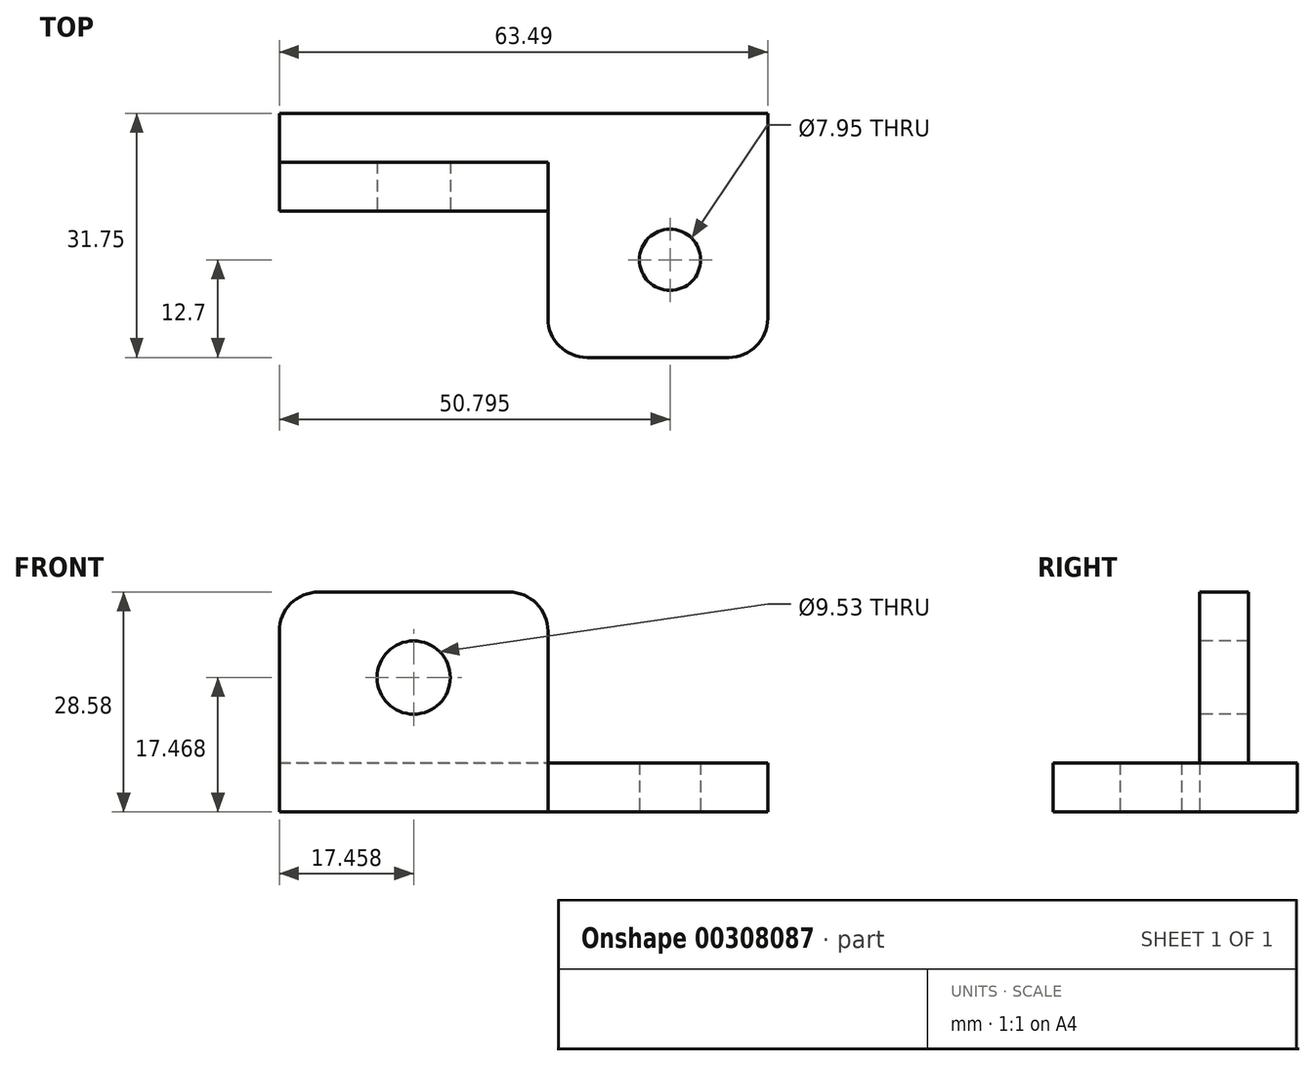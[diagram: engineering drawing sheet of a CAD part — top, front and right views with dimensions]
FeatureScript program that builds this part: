
annotation { "Feature Type Name" : "Feature", "Feature Type Description" : "" }
export const myFeature = defineFeature(function(context is Context, id is Id, definition is map)
    precondition{}
    {
        {
            var Q0;
            Q0=qCreatedBy(makeId("Top.planeOp"),FACE);
            var sketch = newSketch(context, id + "F0", { "sketchPlane" : qUnion([Q0])});
            skLineSegment(sketch, "E0", {"start": v(0, 0) * mm, "end": v(28.57, 0) * mm});
            skLineSegment(sketch, "E1", {"start": v(28.57, 0) * mm, "end": v(28.57, 31.75) * mm});
            skLineSegment(sketch, "E2", {"start": v(28.57, 31.75) * mm, "end": v(-34.92, 31.75) * mm});
            skLineSegment(sketch, "E3", {"start": v(-34.92, 31.75) * mm, "end": v(-34.92, 19.05) * mm});
            skLineSegment(sketch, "E4", {"start": v(-34.92, 19.05) * mm, "end": v(0, 19.05) * mm});
            skLineSegment(sketch, "E5", {"start": v(0, 19.05) * mm, "end": v(0, 0) * mm});
            skCircle(sketch, "E6", {"center": v(15.88, 12.7) * mm, "radius": 3.98 * mm});
            skSolve(sketch);
        }
        {
            var Q0;
            Q0=qSketchRegion(id+"F0",true);
            extrude(context, id + "F1", {"entities" : qUnion([Q0]), "endBound" : BoundingType.SYMMETRIC, "depth" : 6.35 * mm});
        }
        {
            var Q0;
            Q0=makeQuery(id+"F1.opExtrude","SWEPT_FACE",FACE,{"disambiguationData":[OSD([sQuery(id+"F0.wireOp",EDGE,"E4")])]});
            var sketch = newSketch(context, id + "F2", { "sketchPlane" : qUnion([Q0])});
            skLineSegment(sketch, "E7.bottom", {"start": v(-34.92, 3.18) * mm, "end": v(0, 3.18) * mm});
            skLineSegment(sketch, "E7.top", {"start": v(-34.92, 25.4) * mm, "end": v(0, 25.4) * mm});
            skLineSegment(sketch, "E7.left", {"start": v(-34.92, 3.18) * mm, "end": v(-34.92, 25.4) * mm});
            skLineSegment(sketch, "E7.right", {"start": v(0, 3.18) * mm, "end": v(0, 25.4) * mm});
            skCircle(sketch, "E8", {"center": v(-17.46, 14.29) * mm, "radius": 4.76 * mm});
            skSolve(sketch);
        }
        {
            var Q0;
            Q0=qSketchRegion(id+"F2",true);
            extrude(context, id + "F3", {"entities" : qUnion([Q0]), "operationType" : NewBodyOperationType.ADD, "oppositeDirection" : true, "depth" : 6.35 * mm});
        }
        {
            var Q0;
            Q0=makeQuery(id+"F3.opExtrude","SWEPT_EDGE",EDGE,{"disambiguationData":[OSD([sQuery(id+"F2.wireOp",EDGE,"E7.top"),sQuery(id+"F2.wireOp",EDGE,"E7.left")])]});
            var Q1;
            Q1=makeQuery(id+"F3.opExtrude","SWEPT_EDGE",EDGE,{"disambiguationData":[OSD([sQuery(id+"F2.wireOp",EDGE,"E7.top"),sQuery(id+"F2.wireOp",EDGE,"E7.right")])]});
            var Q2;
            Q2=makeQuery(id+"F1.opExtrude","SWEPT_EDGE",EDGE,{"disambiguationData":[OSD([sQuery(id+"F0.wireOp",EDGE,"E0"),sQuery(id+"F0.wireOp",EDGE,"E5")])]});
            var Q3;
            Q3=makeQuery(id+"F1.opExtrude","SWEPT_EDGE",EDGE,{"disambiguationData":[OSD([sQuery(id+"F0.wireOp",EDGE,"E0"),sQuery(id+"F0.wireOp",EDGE,"E1")])]});
            fillet(context, id + "F4", {"entities" : qUnion([Q0, Q1, Q2, Q3]), "radius" : 5.08 * mm, "tangentPropagation" : true, "allowEdgeOverflow" : false});
        }
    });
